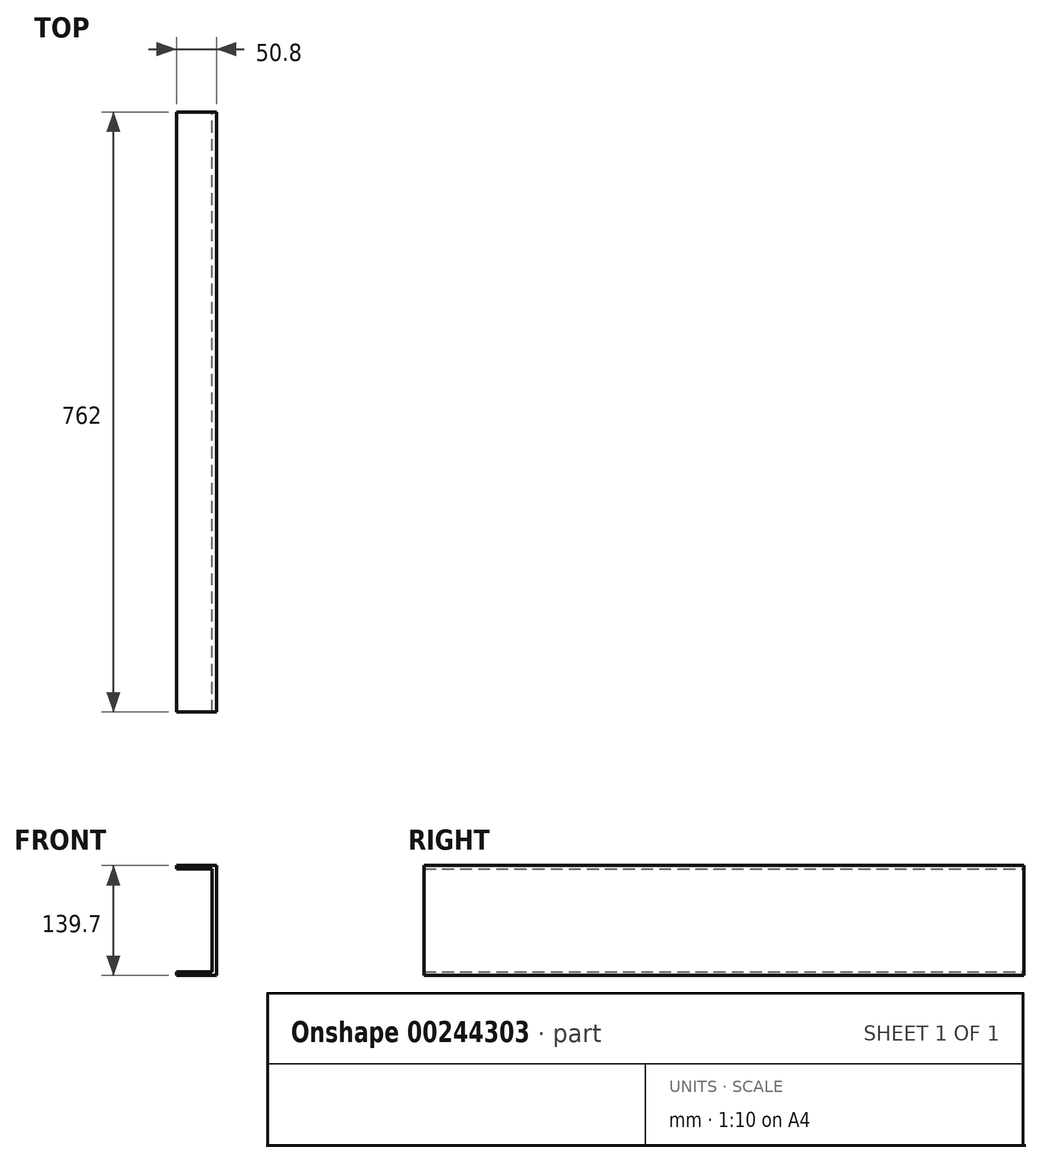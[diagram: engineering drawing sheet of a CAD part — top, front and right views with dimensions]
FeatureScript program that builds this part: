
annotation { "Feature Type Name" : "Feature", "Feature Type Description" : "" }
export const myFeature = defineFeature(function(context is Context, id is Id, definition is map)
    precondition{}
    {
        {
            var Q0;
            Q0=qCreatedBy(makeId("Front.planeOp"),FACE);
            var sketch = newSketch(context, id + "F0", { "sketchPlane" : qUnion([Q0])});
            skLineSegment(sketch, "E0", {"start": v(-5.18, 61.5) * mm, "end": v(45.62, 61.5) * mm});
            skLineSegment(sketch, "E1", {"start": v(45.62, 61.5) * mm, "end": v(45.62, -78.2) * mm});
            skLineSegment(sketch, "E2", {"start": v(45.62, -78.2) * mm, "end": v(-5.18, -78.2) * mm});
            skLineSegment(sketch, "E3", {"start": v(-5.18, 61.5) * mm, "end": v(-5.18, 57.08) * mm});
            skLineSegment(sketch, "E4", {"start": v(-5.18, 57.08) * mm, "end": v(40.28, 57.08) * mm});
            skLineSegment(sketch, "E5", {"start": v(40.28, 57.08) * mm, "end": v(40.28, -73.46) * mm});
            skLineSegment(sketch, "E6", {"start": v(40.28, -73.46) * mm, "end": v(-5.18, -73.46) * mm});
            skLineSegment(sketch, "E7", {"start": v(-5.18, -73.46) * mm, "end": v(-5.18, -78.2) * mm});
            skSolve(sketch);
        }
        {
            var Q0;
            Q0 = qSketchRegion(id + "F0", true);
            extrude(context, id + "F1", {"entities" : qUnion([Q0]), "depth" : 762 * mm});
        }
    });
